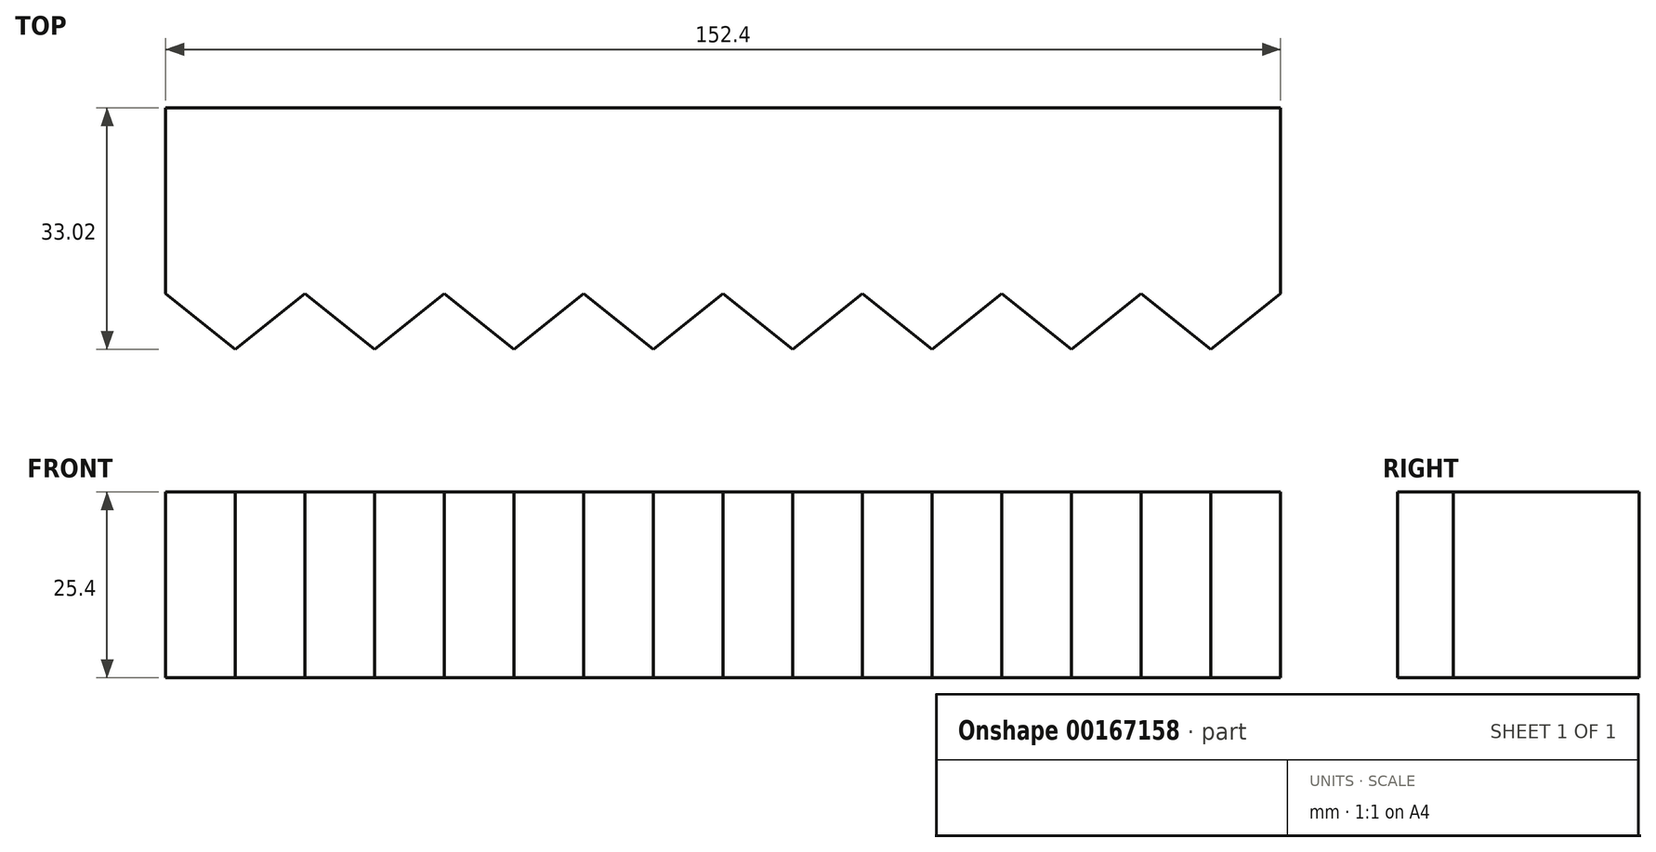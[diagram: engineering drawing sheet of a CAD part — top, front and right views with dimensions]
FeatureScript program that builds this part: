
annotation { "Feature Type Name" : "Feature", "Feature Type Description" : "" }
export const myFeature = defineFeature(function(context is Context, id is Id, definition is map)
    precondition{}
    {
        {
            var Q0;
            Q0=qCreatedBy(makeId("Top.planeOp"),FACE);
            var sketch = newSketch(context, id + "F0", { "sketchPlane" : qUnion([Q0])});
            skLineSegment(sketch, "E0.bottom", {"start": v(76.2, 12.7) * mm, "end": v(-76.2, 12.7) * mm});
            skLineSegment(sketch, "E0.top", {"start": v(76.2, -12.7) * mm, "end": v(-76.2, -12.7) * mm});
            skLineSegment(sketch, "E0.left", {"start": v(76.2, 12.7) * mm, "end": v(76.2, -12.7) * mm});
            skLineSegment(sketch, "E0.right", {"start": v(-76.2, 12.7) * mm, "end": v(-76.2, -12.7) * mm});
            skPoint(sketch, "E0.middle", {"position": v(0, 0) * mm});
            skLineSegment(sketch, "E1", {"start": v(-76.2, -12.7) * mm, "end": v(-66.68, -20.32) * mm});
            skLineSegment(sketch, "E2", {"start": v(-66.68, -20.32) * mm, "end": v(-57.15, -12.7) * mm});
            skLineSegment(sketch, "E3", {"start": v(-57.15, -12.7) * mm, "end": v(-76.2, -12.7) * mm});
            skLineSegment(sketch, "E4", {"start": v(-66.68, -12.7) * mm, "end": v(-66.68, -34.2) * mm, "construction": true});
            skLineSegment(sketch, "E5.1.0.0", {"start": v(-57.15, -12.7) * mm, "end": v(-47.63, -20.32) * mm});
            skLineSegment(sketch, "E5.1.0.1", {"start": v(-47.63, -20.32) * mm, "end": v(-38.1, -12.7) * mm});
            skLineSegment(sketch, "E5.1.0.2", {"start": v(-38.1, -12.7) * mm, "end": v(-57.15, -12.7) * mm});
            skLineSegment(sketch, "E5.2.0.0", {"start": v(-38.1, -12.7) * mm, "end": v(-28.58, -20.32) * mm});
            skLineSegment(sketch, "E5.2.0.1", {"start": v(-28.58, -20.32) * mm, "end": v(-19.05, -12.7) * mm});
            skLineSegment(sketch, "E5.2.0.2", {"start": v(-19.05, -12.7) * mm, "end": v(-38.1, -12.7) * mm});
            skLineSegment(sketch, "E5.3.0.0", {"start": v(-19.05, -12.7) * mm, "end": v(-9.53, -20.32) * mm});
            skLineSegment(sketch, "E5.3.0.1", {"start": v(-9.53, -20.32) * mm, "end": v(0, -12.7) * mm});
            skLineSegment(sketch, "E5.3.0.2", {"start": v(0, -12.7) * mm, "end": v(-19.05, -12.7) * mm});
            skLineSegment(sketch, "E5.4.0.0", {"start": v(0, -12.7) * mm, "end": v(9.52, -20.32) * mm});
            skLineSegment(sketch, "E5.4.0.1", {"start": v(9.52, -20.32) * mm, "end": v(19.05, -12.7) * mm});
            skLineSegment(sketch, "E5.4.0.2", {"start": v(19.05, -12.7) * mm, "end": v(0, -12.7) * mm});
            skLineSegment(sketch, "E5.5.0.0", {"start": v(19.05, -12.7) * mm, "end": v(28.57, -20.32) * mm});
            skLineSegment(sketch, "E5.5.0.1", {"start": v(28.57, -20.32) * mm, "end": v(38.1, -12.7) * mm});
            skLineSegment(sketch, "E5.5.0.2", {"start": v(38.1, -12.7) * mm, "end": v(19.05, -12.7) * mm});
            skLineSegment(sketch, "E5.6.0.0", {"start": v(38.1, -12.7) * mm, "end": v(47.62, -20.32) * mm});
            skLineSegment(sketch, "E5.6.0.1", {"start": v(47.62, -20.32) * mm, "end": v(57.15, -12.7) * mm});
            skLineSegment(sketch, "E5.6.0.2", {"start": v(57.15, -12.7) * mm, "end": v(38.1, -12.7) * mm});
            skLineSegment(sketch, "E5.7.0.0", {"start": v(57.15, -12.7) * mm, "end": v(66.67, -20.32) * mm});
            skLineSegment(sketch, "E5.7.0.1", {"start": v(66.67, -20.32) * mm, "end": v(76.2, -12.7) * mm});
            skLineSegment(sketch, "E5.7.0.2", {"start": v(76.2, -12.7) * mm, "end": v(57.15, -12.7) * mm});
            skLineSegment(sketch, "E5.direction1", {"start": v(-76.2, -12.7) * mm, "end": v(-57.15, -12.7) * mm, "construction": true});
            skSolve(sketch);
        }
        {
            var Q0;
            Q0 = qSketchRegion(id + "F0", true);
            extrude(context, id + "F1", {"entities" : qUnion([Q0]), "depth" : 25.4 * mm});
        }
    });
